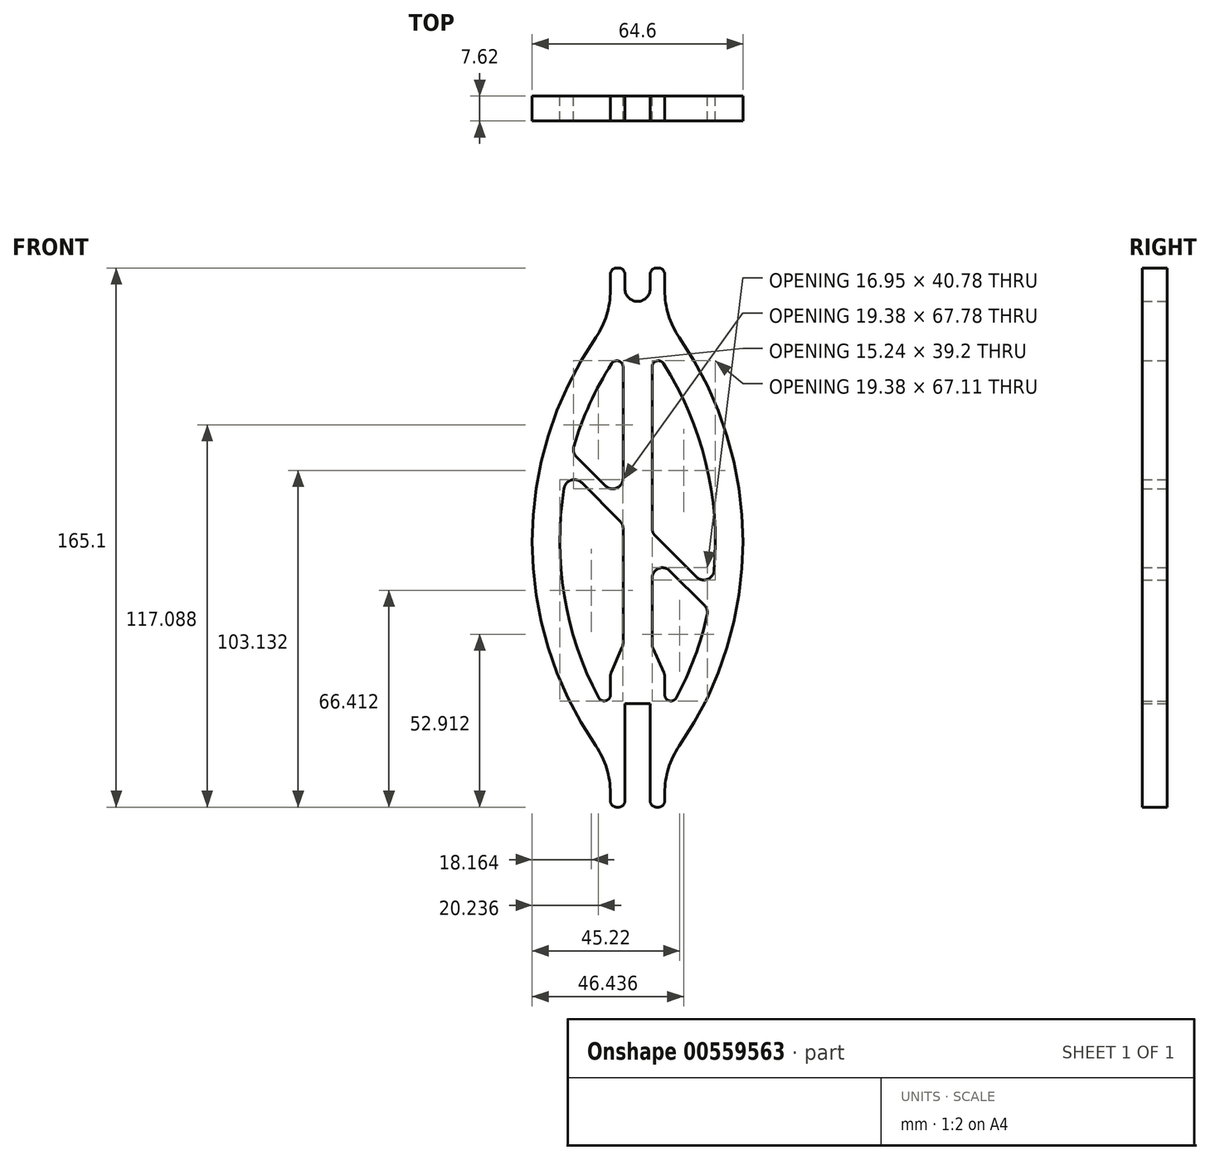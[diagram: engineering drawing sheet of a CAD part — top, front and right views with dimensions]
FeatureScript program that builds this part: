
annotation { "Feature Type Name" : "Feature", "Feature Type Description" : "" }
export const myFeature = defineFeature(function(context is Context, id is Id, definition is map)
    precondition{}
    {
        {
            var Q0;
            Q0=qCreatedBy(makeId("Front.planeOp"),FACE);
            var sketch = newSketch(context, id + "F0", { "sketchPlane" : qUnion([Q0])});
            skLineSegment(sketch, "E0", {"start": v(-3.87, 0) * mm, "end": v(3.87, 0) * mm});
            skLineSegment(sketch, "E1", {"start": v(3.87, 0) * mm, "end": v(3.87, -29.84) * mm});
            skLineSegment(sketch, "E2", {"start": v(-3.87, 0) * mm, "end": v(-3.87, -29.84) * mm});
            skArc(sketch, "E3", {"start": v(-3.87, 127) * mm, "mid": v(0, 123.13) * mm, "end": v(3.87, 127) * mm});
            skLineSegment(sketch, "E4", {"start": v(-3.87, 127) * mm, "end": v(-3.87, 131.44) * mm});
            skLineSegment(sketch, "E5", {"start": v(3.87, 127) * mm, "end": v(3.87, 131.44) * mm});
            skLineSegment(sketch, "E6", {"start": v(-5.78, 133.35) * mm, "end": v(-6.41, 133.35) * mm});
            skLineSegment(sketch, "E7", {"start": v(-8.32, 131.44) * mm, "end": v(-8.32, 126.48) * mm});
            skLineSegment(sketch, "E8", {"start": v(5.78, 133.35) * mm, "end": v(6.41, 133.35) * mm});
            skLineSegment(sketch, "E9", {"start": v(8.32, 131.44) * mm, "end": v(8.32, 126.48) * mm});
            skLineSegment(sketch, "E10", {"start": v(-5.78, -31.75) * mm, "end": v(-6.41, -31.75) * mm});
            skLineSegment(sketch, "E11", {"start": v(-8.32, -29.84) * mm, "end": v(-8.32, -27.42) * mm});
            skLineSegment(sketch, "E12", {"start": v(5.78, -31.75) * mm, "end": v(6.41, -31.75) * mm});
            skLineSegment(sketch, "E13", {"start": v(8.32, -29.84) * mm, "end": v(8.32, -27.42) * mm});
            skLineSegment(sketch, "E14", {"start": v(0, 127) * mm, "end": v(0, 0) * mm, "construction": true});
            skLineSegment(sketch, "E15", {"start": v(-8.32, 118.11) * mm, "end": v(-4.45, 109.22) * mm, "construction": true});
            skLineSegment(sketch, "E16", {"start": v(-4.45, 103.03) * mm, "end": v(-4.45, 68.9) * mm});
            skLineSegment(sketch, "E17", {"start": v(-4.7, 17.17) * mm, "end": v(-8.05, 9.5) * mm});
            skLineSegment(sketch, "E18", {"start": v(8.04, 9.51) * mm, "end": v(4.72, 16.87) * mm});
            skLineSegment(sketch, "E19", {"start": v(4.45, 18.18) * mm, "end": v(4.45, 38.4) * mm});
            skLineSegment(sketch, "E20", {"start": v(4.44, 109.22) * mm, "end": v(8.32, 118.11) * mm, "construction": true});
            skLineSegment(sketch, "E21", {"start": v(-4.45, 109.22) * mm, "end": v(4.45, 109.22) * mm, "construction": true});
            skArc(sketch, "E22", {"start": v(-12.81, 112.05) * mm, "mid": v(-32.3, 49.53) * mm, "end": v(-12.81, -13) * mm});
            skArc(sketch, "E23", {"start": v(-7.96, 104.06) * mm, "mid": v(-14.63, 91.78) * mm, "end": v(-19.55, 78.7) * mm});
            skArc(sketch, "E24.MirrorCS", {"start": v(12.81, 112.05) * mm, "mid": v(32.3, 49.53) * mm, "end": v(12.81, -13) * mm});
            skArc(sketch, "E25.MirrorCS", {"start": v(7.96, 104.06) * mm, "mid": v(20.92, 73.66) * mm, "end": v(23.45, 40.72) * mm});
            skLineSegment(sketch, "E26.trimOffspring", {"start": v(-8.32, 2.67) * mm, "end": v(-8.32, 8.23) * mm});
            skLineSegment(sketch, "E27.trimOffspring", {"start": v(8.32, 2.67) * mm, "end": v(8.32, 8.2) * mm});
            skLineSegment(sketch, "E28", {"start": v(-18.75, 75.54) * mm, "end": v(-9.87, 66.65) * mm});
            skLineSegment(sketch, "E29", {"start": v(-17.12, 67.63) * mm, "end": v(-5.37, 55.88) * mm});
            skLineSegment(sketch, "E30", {"start": v(-23.77, 53) * mm, "end": v(23.77, 53) * mm, "construction": true});
            skLineSegment(sketch, "E31", {"start": v(-21.35, 71.85) * mm, "end": v(-21.35, 53) * mm, "construction": true});
            skLineSegment(sketch, "E32", {"start": v(22.65, 34.13) * mm, "end": v(22.65, 53) * mm, "construction": true});
            skArc(sketch, "E33.trimOffspring", {"start": v(-22.5, 65.9) * mm, "mid": v(-22.47, 32.96) * mm, "end": v(-11.9, 1.77) * mm});
            skLineSegment(sketch, "E34.trimOffspring", {"start": v(-4.44, 53.63) * mm, "end": v(-4.44, 18.44) * mm});
            skLineSegment(sketch, "E35.trimOffspring", {"start": v(5.37, 51.41) * mm, "end": v(18.04, 38.75) * mm});
            skLineSegment(sketch, "E36.trimOffspring", {"start": v(9.87, 40.64) * mm, "end": v(20.47, 30.04) * mm});
            skLineSegment(sketch, "E37.trimOffspring", {"start": v(4.45, 53.66) * mm, "end": v(4.45, 103.03) * mm});
            skArc(sketch, "E38.trimOffspring", {"start": v(21.32, 27.09) * mm, "mid": v(17.46, 14.12) * mm, "end": v(11.9, 1.77) * mm});
            skPoint(sketch, "E39.visualSharp", {"position": v(-8.32, -19.05) * mm});
            skArc(sketch, "E39.filletArc", {"start": v(-8.32, -27.42) * mm, "mid": v(-9.47, -19.86) * mm, "end": v(-12.81, -13) * mm});
            skPoint(sketch, "E40.visualSharp", {"position": v(8.32, -19.05) * mm});
            skArc(sketch, "E40.filletArc", {"start": v(12.81, -13) * mm, "mid": v(9.47, -19.86) * mm, "end": v(8.32, -27.42) * mm});
            skPoint(sketch, "E41.visualSharp", {"position": v(-8.32, 118.11) * mm});
            skArc(sketch, "E41.filletArc", {"start": v(-12.81, 112.05) * mm, "mid": v(-9.47, 118.92) * mm, "end": v(-8.32, 126.48) * mm});
            skPoint(sketch, "E42.visualSharp", {"position": v(8.32, 118.11) * mm});
            skArc(sketch, "E42.filletArc", {"start": v(8.32, 126.48) * mm, "mid": v(9.47, 118.92) * mm, "end": v(12.81, 112.05) * mm});
            skPoint(sketch, "E43.visualSharp", {"position": v(-3.87, -31.75) * mm});
            skArc(sketch, "E43.filletArc", {"start": v(-5.78, -31.75) * mm, "mid": v(-4.43, -31.2) * mm, "end": v(-3.87, -29.84) * mm});
            skPoint(sketch, "E44.visualSharp", {"position": v(-8.32, -31.75) * mm});
            skArc(sketch, "E44.filletArc", {"start": v(-8.32, -29.84) * mm, "mid": v(-7.76, -31.2) * mm, "end": v(-6.41, -31.75) * mm});
            skPoint(sketch, "E45.visualSharp", {"position": v(3.87, -31.75) * mm});
            skArc(sketch, "E45.filletArc", {"start": v(3.87, -29.84) * mm, "mid": v(4.43, -31.2) * mm, "end": v(5.78, -31.75) * mm});
            skPoint(sketch, "E46.visualSharp", {"position": v(8.32, -31.75) * mm});
            skArc(sketch, "E46.filletArc", {"start": v(6.41, -31.75) * mm, "mid": v(7.76, -31.2) * mm, "end": v(8.32, -29.84) * mm});
            skPoint(sketch, "E47.visualSharp", {"position": v(-8.32, -4.42) * mm});
            skArc(sketch, "E47.filletArc", {"start": v(-11.9, 1.77) * mm, "mid": v(-9.76, 0.82) * mm, "end": v(-8.32, 2.67) * mm});
            skPoint(sketch, "E48.visualSharp", {"position": v(8.32, -4.42) * mm});
            skArc(sketch, "E48.filletArc", {"start": v(8.32, 2.67) * mm, "mid": v(9.76, 0.82) * mm, "end": v(11.9, 1.77) * mm});
            skPoint(sketch, "E49.visualSharp", {"position": v(-4.45, 109.22) * mm});
            skArc(sketch, "E49.filletArc", {"start": v(-4.45, 103.03) * mm, "mid": v(-5.82, 104.86) * mm, "end": v(-7.96, 104.06) * mm});
            skPoint(sketch, "E50.visualSharp", {"position": v(4.45, 109.22) * mm});
            skArc(sketch, "E50.filletArc", {"start": v(7.96, 104.06) * mm, "mid": v(5.82, 104.86) * mm, "end": v(4.45, 103.03) * mm});
            skPoint(sketch, "E51.visualSharp", {"position": v(-8.32, 133.35) * mm});
            skArc(sketch, "E51.filletArc", {"start": v(-6.41, 133.35) * mm, "mid": v(-7.76, 132.8) * mm, "end": v(-8.32, 131.44) * mm});
            skPoint(sketch, "E52.visualSharp", {"position": v(-3.87, 133.35) * mm});
            skArc(sketch, "E52.filletArc", {"start": v(-3.87, 131.44) * mm, "mid": v(-4.43, 132.8) * mm, "end": v(-5.78, 133.35) * mm});
            skPoint(sketch, "E53.visualSharp", {"position": v(3.87, 133.35) * mm});
            skArc(sketch, "E53.filletArc", {"start": v(5.78, 133.35) * mm, "mid": v(4.43, 132.8) * mm, "end": v(3.87, 131.44) * mm});
            skPoint(sketch, "E54.visualSharp", {"position": v(8.32, 133.35) * mm});
            skArc(sketch, "E54.filletArc", {"start": v(8.32, 131.44) * mm, "mid": v(7.76, 132.8) * mm, "end": v(6.41, 133.35) * mm});
            skPoint(sketch, "E55.visualSharp", {"position": v(4.45, 17.5) * mm});
            skArc(sketch, "E55.filletArc", {"start": v(4.44, 18.18) * mm, "mid": v(4.52, 17.51) * mm, "end": v(4.72, 16.87) * mm});
            skPoint(sketch, "E56.visualSharp", {"position": v(-4.44, 17.78) * mm});
            skArc(sketch, "E56.filletArc", {"start": v(-4.7, 17.17) * mm, "mid": v(-4.51, 17.8) * mm, "end": v(-4.45, 18.44) * mm});
            skPoint(sketch, "E57.visualSharp", {"position": v(-8.32, 8.89) * mm});
            skArc(sketch, "E57.filletArc", {"start": v(-8.05, 9.5) * mm, "mid": v(-8.25, 8.88) * mm, "end": v(-8.32, 8.23) * mm});
            skPoint(sketch, "E58.visualSharp", {"position": v(8.32, 8.89) * mm});
            skArc(sketch, "E58.filletArc", {"start": v(8.32, 8.2) * mm, "mid": v(8.25, 8.87) * mm, "end": v(8.04, 9.51) * mm});
            skPoint(sketch, "E59.visualSharp", {"position": v(21.7, 28.8) * mm});
            skArc(sketch, "E59.filletArc", {"start": v(21.32, 27.09) * mm, "mid": v(21.27, 28.67) * mm, "end": v(20.47, 30.04) * mm});
            skPoint(sketch, "E60.visualSharp", {"position": v(22.65, 34.13) * mm});
            skArc(sketch, "E60.filletArc", {"start": v(18.04, 38.75) * mm, "mid": v(21.37, 38.01) * mm, "end": v(23.45, 40.72) * mm});
            skPoint(sketch, "E61.visualSharp", {"position": v(4.45, 46.06) * mm});
            skArc(sketch, "E61.filletArc", {"start": v(9.87, 40.64) * mm, "mid": v(6.4, 41.33) * mm, "end": v(4.44, 38.4) * mm});
            skPoint(sketch, "E62.visualSharp", {"position": v(4.44, 52.34) * mm});
            skArc(sketch, "E62.filletArc", {"start": v(4.44, 53.66) * mm, "mid": v(4.69, 52.44) * mm, "end": v(5.37, 51.41) * mm});
            skPoint(sketch, "E63.visualSharp", {"position": v(-4.44, 54.95) * mm});
            skArc(sketch, "E63.filletArc", {"start": v(-4.44, 53.63) * mm, "mid": v(-4.69, 54.85) * mm, "end": v(-5.37, 55.88) * mm});
            skPoint(sketch, "E64.visualSharp", {"position": v(-4.45, 61.23) * mm});
            skArc(sketch, "E64.filletArc", {"start": v(-9.87, 66.65) * mm, "mid": v(-6.4, 65.97) * mm, "end": v(-4.45, 68.9) * mm});
            skPoint(sketch, "E65.visualSharp", {"position": v(-21.35, 71.85) * mm});
            skArc(sketch, "E65.filletArc", {"start": v(-17.12, 67.63) * mm, "mid": v(-20.34, 68.4) * mm, "end": v(-22.5, 65.9) * mm});
            skPoint(sketch, "E66.visualSharp", {"position": v(-20.08, 76.87) * mm});
            skArc(sketch, "E66.filletArc", {"start": v(-19.55, 78.7) * mm, "mid": v(-19.59, 77.01) * mm, "end": v(-18.75, 75.54) * mm});
            skSolve(sketch);
        }
        {
            var Q0;
            Q0=makeQuery(id+"F0.imprint","IMPRINT",FACE,{"disambiguationData":[TD([[makeQuery(id+"F0.imprint","IMPRINT",EDGE,{"derivedFrom":sQuery(id+"F0.wireOp",EDGE,"E0")}),1.0]])]});
            extrude(context, id + "F1", {"entities" : qUnion([Q0]), "depth" : 7.62 * mm, "offsetDistance" : 25.4 * mm});
        }
    });
